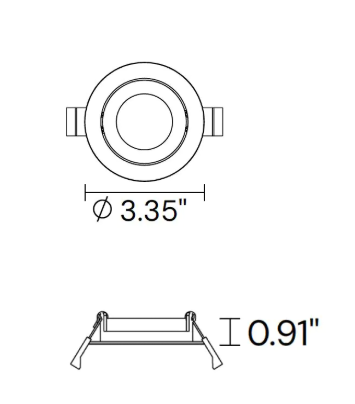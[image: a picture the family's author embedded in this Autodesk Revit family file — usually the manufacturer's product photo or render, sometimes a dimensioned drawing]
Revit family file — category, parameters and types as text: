
# Revit family: Alcon-14119-R-ADJ-Revit-Family
name_source: partatom
category: Lighting Fixtures
units: mm (PartAtom-declared; Revit-internal decimal feet)

## family parameters
Always vertical = Yes
Cut with Voids When Loaded = No
Host = Ceiling
Light Source = Yes
OmniClass Number = 23.80.70.11
OmniClass Title = Luminaries for Internal Lighting
Part Type = Normal
Room Calculation Point = No
Round Connector Dimension = Use Diameter
Shared = No

## types (1)
- Type 1
    Color Filter = 16777215
    Default Elevation = 0' - 0"
    Dimming Lamp Color Temperature Shift = <None>
    Housing = <By Category>
    Lens = <By Category>
    Light Source Symbol Length = 10' - 0"
    LightSource = <By Category>
    Link To Product Page = https://www.alconlighting.com
    Manufacturer = Alcon Light
    Metal = <By Category>
    Product Identity = Alcon Lighting 14119-R-ADJ
    Spot Beam Angle = 30.00°
    Spot Field Angle = 90.00°
    Tilt Angle = 60.00°

## geometry (parser evidence)
native form markers: Sweep x2
no freeform markers — native parametric forms only
